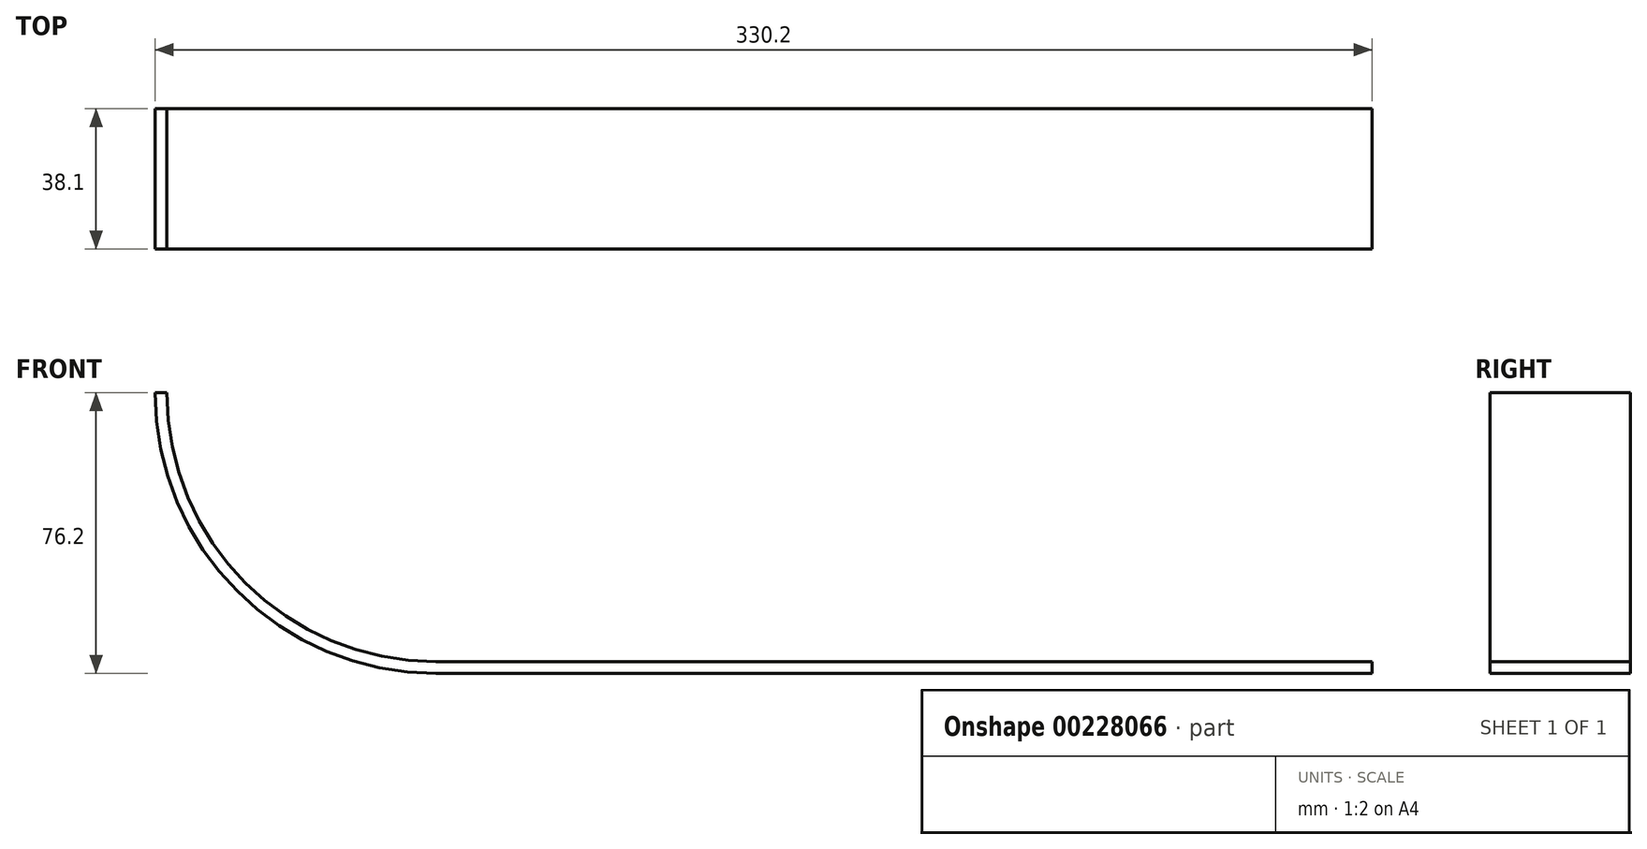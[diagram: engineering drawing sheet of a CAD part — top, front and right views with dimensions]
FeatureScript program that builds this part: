
annotation { "Feature Type Name" : "Feature", "Feature Type Description" : "" }
export const myFeature = defineFeature(function(context is Context, id is Id, definition is map)
    precondition{}
    {
        {
            var Q0;
            Q0=qCreatedBy(makeId("Front.planeOp"),FACE);
            var sketch = newSketch(context, id + "F0", { "sketchPlane" : qUnion([Q0])});
            skLineSegment(sketch, "E0", {"start": v(0, 0) * mm, "end": v(-254, 0) * mm});
            skArc(sketch, "E1", {"start": v(-254, 0) * mm, "mid": v(-307.88, 22.32) * mm, "end": v(-330.2, 76.2) * mm});
            skArc(sketch, "E2.0", {"start": v(-254, 3.17) * mm, "mid": v(-305.64, 24.56) * mm, "end": v(-327.03, 76.2) * mm});
            skLineSegment(sketch, "E2.1", {"start": v(0, 3.17) * mm, "end": v(-254, 3.17) * mm});
            skLineSegment(sketch, "E3", {"start": v(-327.03, 76.2) * mm, "end": v(-330.2, 76.2) * mm});
            skLineSegment(sketch, "E4", {"start": v(0, 3.17) * mm, "end": v(0, 0) * mm});
            skSolve(sketch);
        }
        {
            var Q0;
            Q0 = qSketchRegion(id + "F0", true);
            extrude(context, id + "F1", {"entities" : qUnion([Q0]), "depth" : 38.1 * mm});
        }
    });
